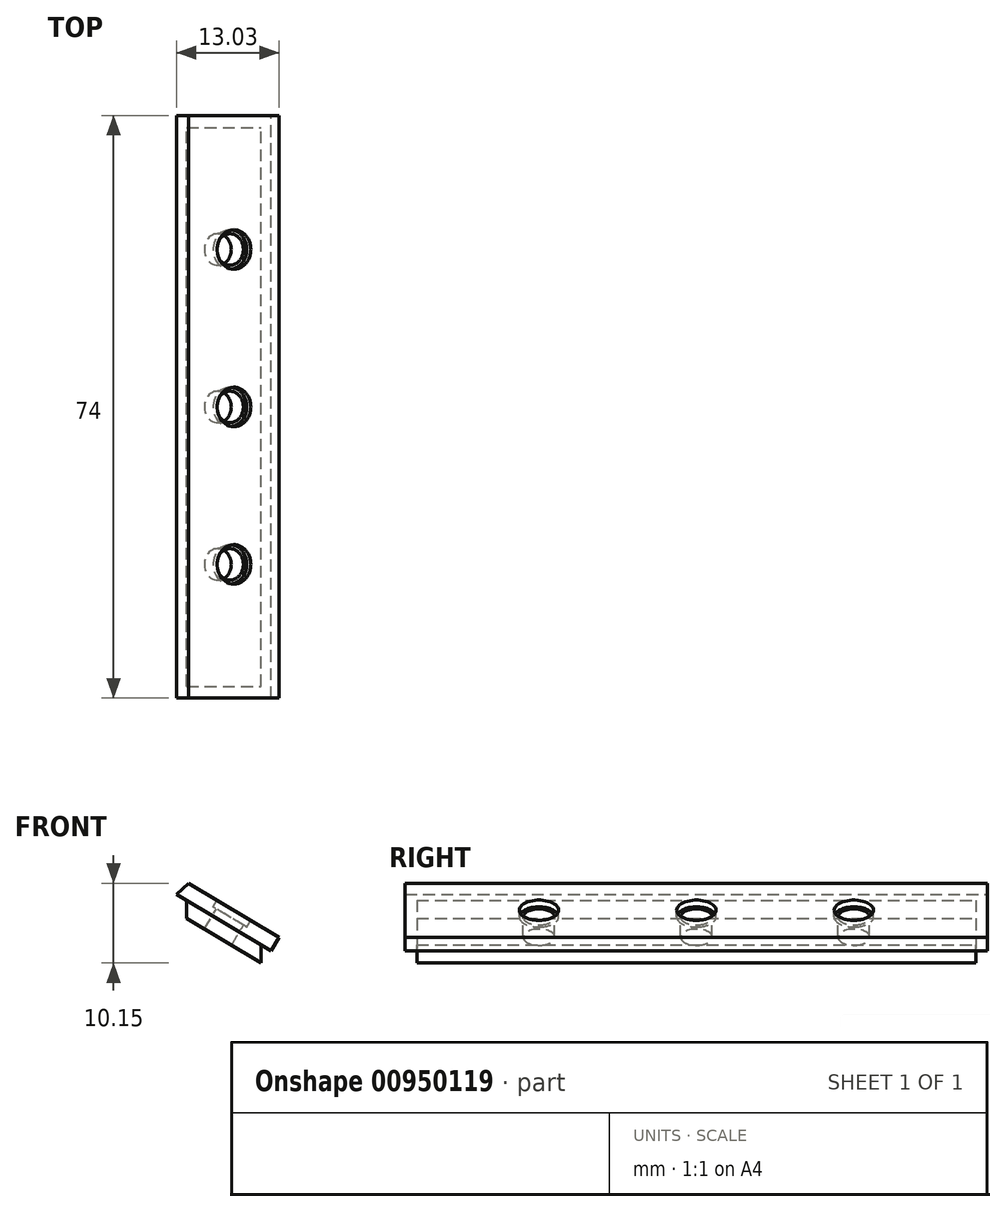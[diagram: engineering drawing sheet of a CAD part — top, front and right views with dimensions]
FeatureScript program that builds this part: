
annotation { "Feature Type Name" : "Feature", "Feature Type Description" : "" }
export const myFeature = defineFeature(function(context is Context, id is Id, definition is map)
    precondition{}
    {
        {
            var Q0;
            Q0=qCreatedBy(makeId("Front.planeOp"),FACE);
            var sketch = newSketch(context, id + "F0", { "sketchPlane" : qUnion([Q0])});
            skLineSegment(sketch, "E0", {"start": v(0, 0) * mm, "end": v(-11.48, 6.87) * mm});
            skLineSegment(sketch, "E1", {"start": v(-12, 7.18) * mm, "end": v(-13.03, 5.47) * mm, "construction": true});
            skLineSegment(sketch, "E2", {"start": v(-13.03, 5.47) * mm, "end": v(-1.03, -1.72) * mm});
            skLineSegment(sketch, "E3", {"start": v(-1.03, -1.72) * mm, "end": v(0, 0) * mm});
            skLineSegment(sketch, "E4", {"start": v(-11.74, 4.7) * mm, "end": v(-10.71, 6.41) * mm, "construction": true});
            skLineSegment(sketch, "E5", {"start": v(-2.31, -0.95) * mm, "end": v(-1.29, 0.77) * mm, "construction": true});
            skLineSegment(sketch, "E6", {"start": v(-11.74, 4.7) * mm, "end": v(-11.74, 2.36) * mm});
            skLineSegment(sketch, "E7", {"start": v(-11.74, 2.36) * mm, "end": v(-2.31, -3.28) * mm});
            skLineSegment(sketch, "E8", {"start": v(-2.31, -3.28) * mm, "end": v(-2.31, -0.95) * mm});
            skLineSegment(sketch, "E9", {"start": v(-13.03, 5.47) * mm, "end": v(-11.48, 6.87) * mm});
            skLineSegment(sketch, "E10", {"start": v(-11.48, 6.87) * mm, "end": v(-12, 7.18) * mm, "construction": true});
            skSolve(sketch);
        }
        {
            var Q0;
            Q0=makeQuery(id+"F0.imprint","IMPRINT",FACE,{"disambiguationData":[TD([[makeQuery(id+"F0.imprint","IMPRINT",EDGE,{"derivedFrom":sQuery(id+"F0.wireOp",EDGE,"E0")}),1.0]])]});
            extrude(context, id + "F1", {"entities" : qUnion([Q0]), "endBound" : BoundingType.SYMMETRIC, "depth" : 74 * mm, "offsetDistance" : 25 * mm});
        }
        {
            var Q0;
            {var subQ0=sQuery(id+"F0.wireOp",EDGE,"E6");Q0=makeQuery(id+"F0.imprint","IMPRINT",FACE,{"disambiguationData":[TD([[makeQuery(id+"F0.imprint","IMPRINT",EDGE,{"derivedFrom":subQ0}),1.0]])]});}
            extrude(context, id + "F2", {"entities" : qUnion([Q0]), "operationType" : NewBodyOperationType.ADD, "endBound" : BoundingType.SYMMETRIC, "depth" : 71 * mm, "offsetDistance" : 25 * mm});
        }
        {
            var Q0;
            Q0=makeQuery(id+"F1.opExtrude","SWEPT_FACE",FACE,{"disambiguationData":[OSD([sQuery(id+"F0.wireOp",EDGE,"E0")])]});
            var sketch = newSketch(context, id + "F3", { "sketchPlane" : qUnion([Q0])});
            skCircle(sketch, "E11", {"center": v(-6.69, 0) * mm, "radius": 2.5 * mm});
            skCircle(sketch, "E12", {"center": v(-6.69, 20) * mm, "radius": 2.5 * mm});
            skCircle(sketch, "E13", {"center": v(-6.69, -20) * mm, "radius": 2.5 * mm});
            skPoint(sketch, "E14.endSnap0", {"position": v(-6.69, -37) * mm});
            skLineSegment(sketch, "E15", {"start": v(0, 0) * mm, "end": v(0, 0) * mm});
            skLineSegment(sketch, "E16", {"start": v(-6.69, 37) * mm, "end": v(-6.69, -37) * mm, "construction": true});
            skSolve(sketch);
        }
        {
            var Q0;
            Q0=sQuery(id+"F3.wireOp",VERTEX,"E12.center");
            var Q1;
            Q1=sQuery(id+"F3.wireOp",VERTEX,"E11.center");
            var Q2;
            Q2=sQuery(id+"F3.wireOp",VERTEX,"E13.center");
            var Q3;
            Q3=makeQuery(id+"F1.opExtrude","SWEPT_BODY",BODY,{"disambiguationData":[OSD([sQuery(id+"F0.wireOp",EDGE,"E0"),sQuery(id+"F0.wireOp",EDGE,"E1"),sQuery(id+"F0.wireOp",EDGE,"E2"),sQuery(id+"F0.wireOp",EDGE,"E3")])]});
            hole(context, id + "F4", {"style" : HoleStyle.C_BORE, "endStyle" : HoleEndStyle.BLIND, "holeDiameter" : 4 * mm, "cBoreDiameter" : 5 * mm, "cBoreDepth" : 1 * mm, "majorDiameter" : 5 * mm, "holeDepth" : 5 * mm, "isTappedThrough" : true, "tappedDepth" : 12 * mm, "tapClearance" : 3, "locations" : qUnion([Q0, Q1, Q2]), "scope" : qUnion([Q3])});
        }
    });
